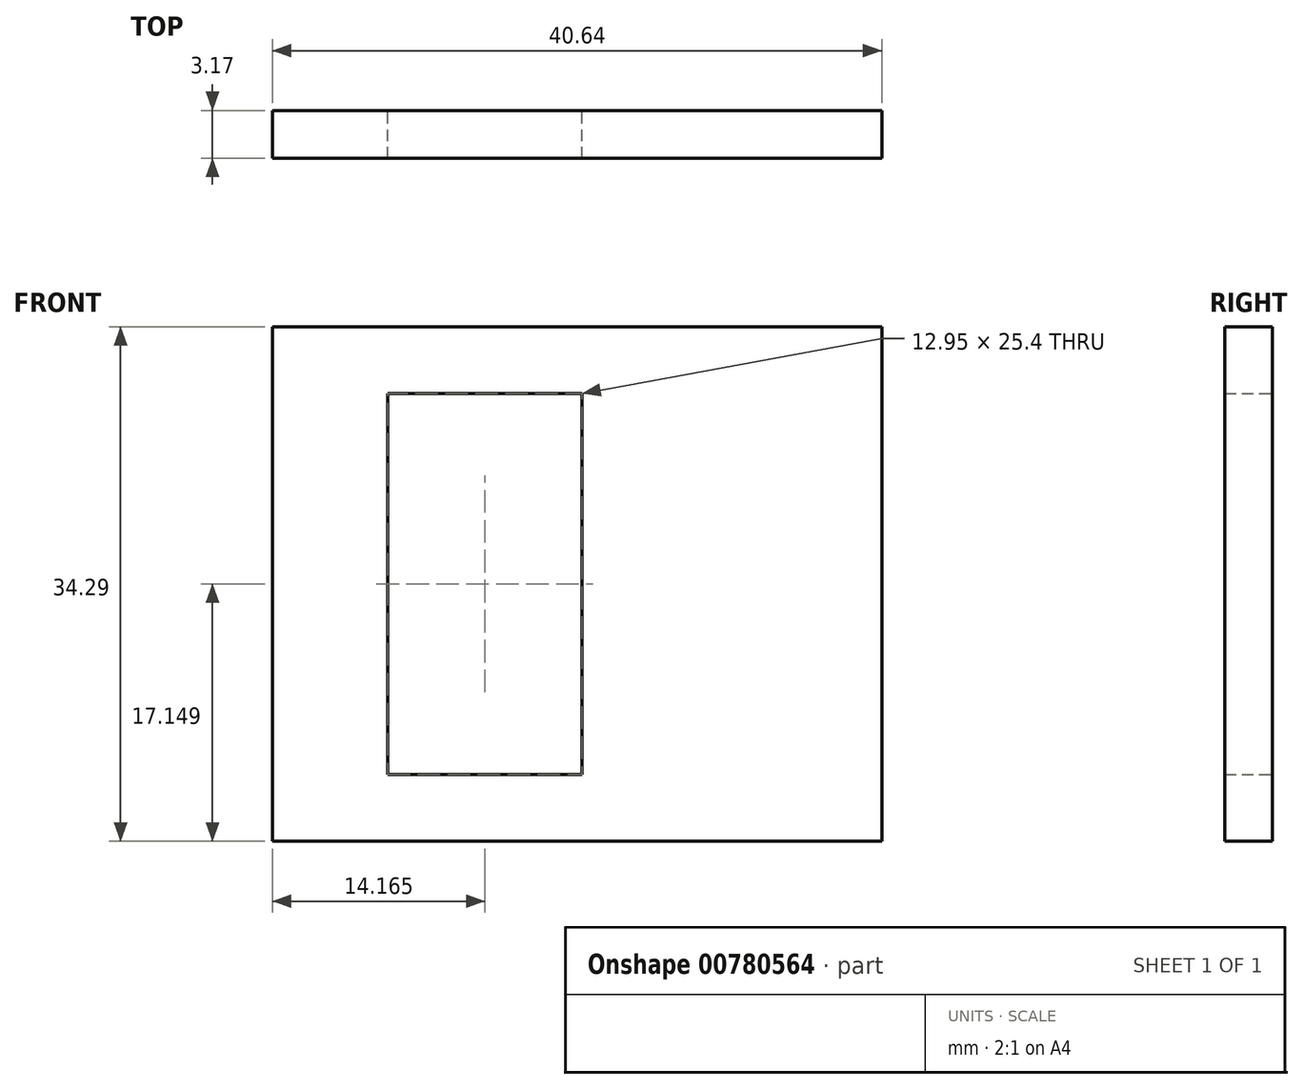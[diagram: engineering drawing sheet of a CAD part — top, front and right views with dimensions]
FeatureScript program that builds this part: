
annotation { "Feature Type Name" : "Feature", "Feature Type Description" : "" }
export const myFeature = defineFeature(function(context is Context, id is Id, definition is map)
    precondition{}
    {
        {
            var Q0;
            Q0=qCreatedBy(makeId("Front.planeOp"),FACE);
            var sketch = newSketch(context, id + "F0", { "sketchPlane" : qUnion([Q0])});
            skLineSegment(sketch, "E0.bottom", {"start": v(74.21, 33.32) * mm, "end": v(114.85, 33.32) * mm});
            skLineSegment(sketch, "E0.top", {"start": v(74.21, -0.97) * mm, "end": v(114.85, -0.97) * mm});
            skLineSegment(sketch, "E0.left", {"start": v(74.21, 33.32) * mm, "end": v(74.21, -0.97) * mm});
            skLineSegment(sketch, "E0.right", {"start": v(114.85, 33.32) * mm, "end": v(114.85, -0.97) * mm});
            skLineSegment(sketch, "E1.bottom", {"start": v(81.9, 28.88) * mm, "end": v(94.85, 28.88) * mm});
            skLineSegment(sketch, "E1.top", {"start": v(81.9, 3.48) * mm, "end": v(94.85, 3.48) * mm});
            skLineSegment(sketch, "E1.left", {"start": v(81.9, 28.88) * mm, "end": v(81.9, 3.48) * mm});
            skLineSegment(sketch, "E1.right", {"start": v(94.85, 28.88) * mm, "end": v(94.85, 3.48) * mm});
            skSolve(sketch);
        }
        {
            var Q0;
            Q0=makeQuery(id+"F0.imprint","IMPRINT",FACE,{"disambiguationData":[TD([[makeQuery(id+"F0.imprint","IMPRINT",EDGE,{"derivedFrom":sQuery(id+"F0.wireOp",EDGE,"E0.bottom")}),-1.0]])]});
            extrude(context, id + "F1", {"entities" : qUnion([Q0]), "depth" : 3.17 * mm, "offsetDistance" : 25.4 * mm});
        }
    });
